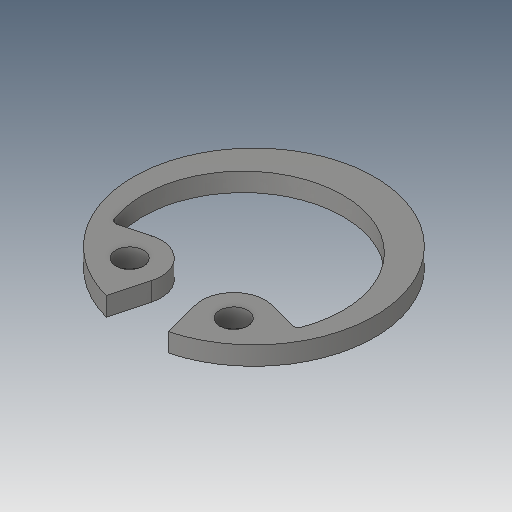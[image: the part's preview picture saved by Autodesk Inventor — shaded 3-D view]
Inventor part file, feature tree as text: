
AUTODESK INVENTOR PART (.ipt)
format: ipt  version: 2019 (Build 230136000, 136)  size: 108,544 bytes
history: native  units: mm
features: fillet x1
ambient origin geometry x8: Origin, YZ Plane, XZ Plane, XY Plane, X Axis, Y Axis, Z Axis, Center Point
bodies: Solid1 (feature_tree)
feature tree (1):
  fillet  "Fillet1"  [1 undecoded]
note: 1 required parameter value undecoded (feature->parameter linkage not recoverable at this tier; creation-order binding heuristic only, values carry confidence <= 0.55)
